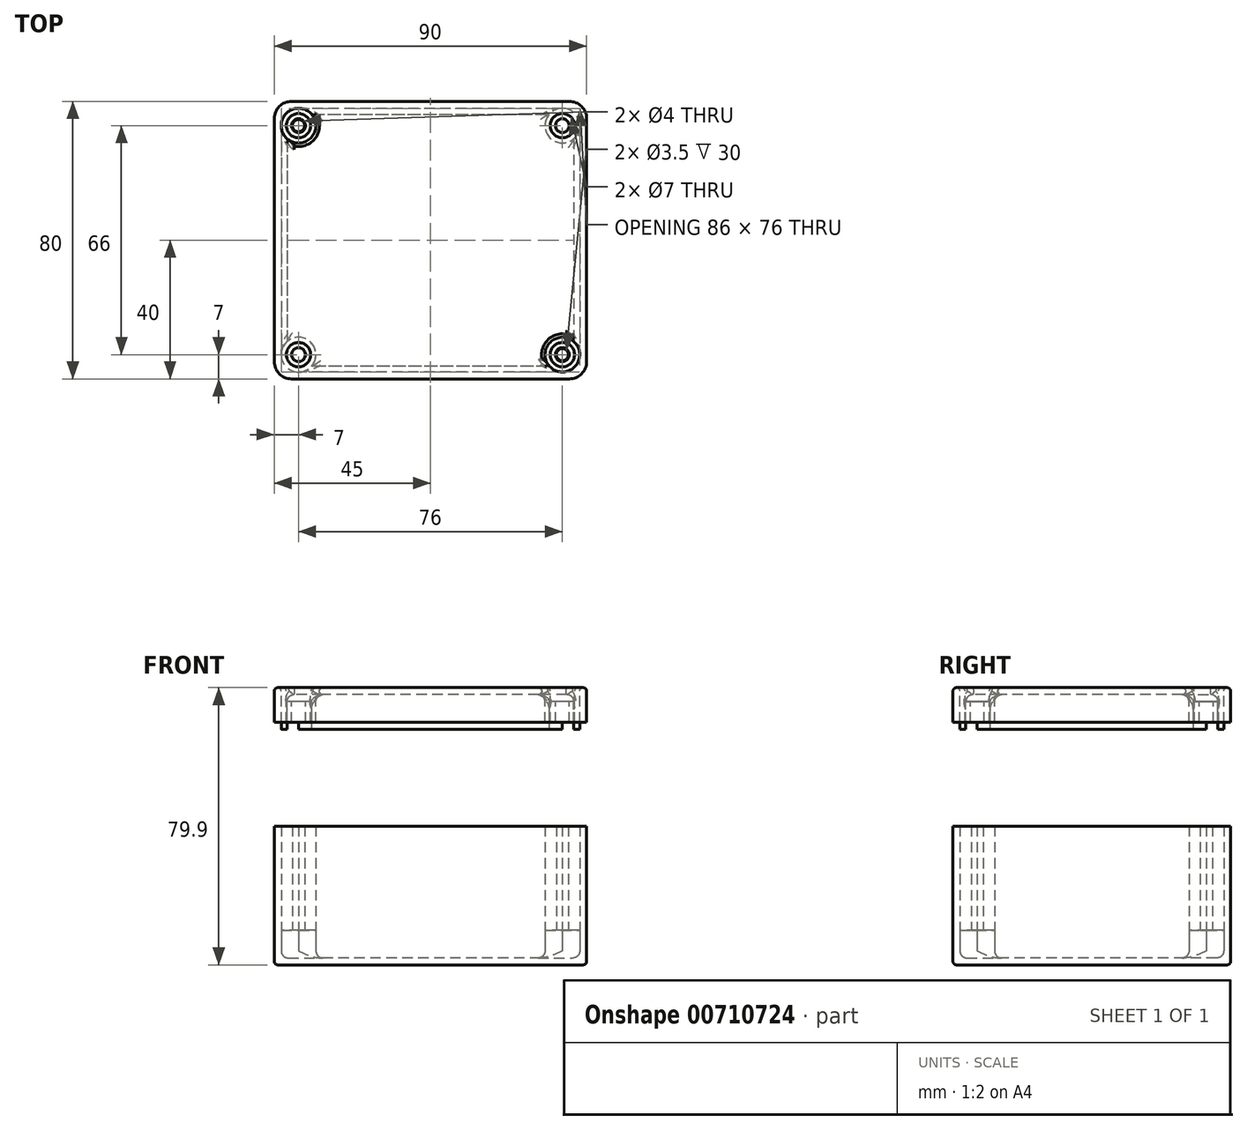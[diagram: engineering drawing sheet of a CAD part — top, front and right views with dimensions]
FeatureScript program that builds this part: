
annotation { "Feature Type Name" : "Feature", "Feature Type Description" : "" }
export const myFeature = defineFeature(function(context is Context, id is Id, definition is map)
    precondition{}
    {
        {
            var Q0;
            Q0=qCreatedBy(makeId("Top.planeOp"),FACE);
            var sketch = newSketch(context, id + "F0", { "sketchPlane" : qUnion([Q0])});
            skLineSegment(sketch, "E0.bottom", {"start": v(40, 40) * mm, "end": v(-40, 40) * mm});
            skLineSegment(sketch, "E0.top", {"start": v(40, -40) * mm, "end": v(-40, -40) * mm});
            skLineSegment(sketch, "E0.left", {"start": v(45, 35) * mm, "end": v(45, -35) * mm});
            skLineSegment(sketch, "E0.right", {"start": v(-45, 35) * mm, "end": v(-45, -35) * mm});
            skPoint(sketch, "E0.middle", {"position": v(0, 0) * mm});
            skPoint(sketch, "E1.visualSharp", {"position": v(-45, 40) * mm});
            skArc(sketch, "E1.filletArc", {"start": v(-40, 40) * mm, "mid": v(-43.54, 38.54) * mm, "end": v(-45, 35) * mm});
            skPoint(sketch, "E2.visualSharp", {"position": v(45, 40) * mm});
            skArc(sketch, "E2.filletArc", {"start": v(45, 35) * mm, "mid": v(43.54, 38.54) * mm, "end": v(40, 40) * mm});
            skPoint(sketch, "E3.visualSharp", {"position": v(-45, -40) * mm});
            skArc(sketch, "E3.filletArc", {"start": v(-45, -35) * mm, "mid": v(-43.54, -38.54) * mm, "end": v(-40, -40) * mm});
            skPoint(sketch, "E4.visualSharp", {"position": v(45, -40) * mm});
            skArc(sketch, "E4.filletArc", {"start": v(40, -40) * mm, "mid": v(43.54, -38.54) * mm, "end": v(45, -35) * mm});
            skLineSegment(sketch, "E5.0", {"start": v(38, -38) * mm, "end": v(-38, -38) * mm});
            skLineSegment(sketch, "E5.1", {"start": v(43, 33) * mm, "end": v(43, -33) * mm});
            skLineSegment(sketch, "E5.2", {"start": v(38, 38) * mm, "end": v(-38, 38) * mm});
            skLineSegment(sketch, "E5.3", {"start": v(-43, 33) * mm, "end": v(-43, -33) * mm});
            skPoint(sketch, "E6.visualSharp", {"position": v(43, 38) * mm});
            skArc(sketch, "E6.filletArc", {"start": v(43, 33) * mm, "mid": v(41.54, 36.54) * mm, "end": v(38, 38) * mm});
            skPoint(sketch, "E7.visualSharp", {"position": v(43, -38) * mm});
            skArc(sketch, "E7.filletArc", {"start": v(38, -38) * mm, "mid": v(41.54, -36.54) * mm, "end": v(43, -33) * mm});
            skPoint(sketch, "E8.visualSharp", {"position": v(-43, -38) * mm});
            skArc(sketch, "E8.filletArc", {"start": v(-43, -33) * mm, "mid": v(-41.54, -36.54) * mm, "end": v(-38, -38) * mm});
            skPoint(sketch, "E9.visualSharp", {"position": v(-43, 38) * mm});
            skArc(sketch, "E9.filletArc", {"start": v(-38, 38) * mm, "mid": v(-41.54, 36.54) * mm, "end": v(-43, 33) * mm});
            skLineSegment(sketch, "E10", {"start": v(0, 38) * mm, "end": v(0, -38) * mm, "construction": true});
            skCircle(sketch, "E11", {"center": v(-38, 33) * mm, "radius": 5 * mm});
            skCircle(sketch, "E12", {"center": v(-38, 33) * mm, "radius": 1.75 * mm});
            skLineSegment(sketch, "E13", {"start": v(-43, 0) * mm, "end": v(43, 0) * mm, "construction": true});
            skCircle(sketch, "E14.MirrorC", {"center": v(-38, -33) * mm, "radius": 5 * mm});
            skCircle(sketch, "E15.MirrorC", {"center": v(-38, -33) * mm, "radius": 1.75 * mm});
            skCircle(sketch, "E16.MirrorC", {"center": v(38, 33) * mm, "radius": 5 * mm});
            skCircle(sketch, "E17.MirrorC", {"center": v(38, 33) * mm, "radius": 1.75 * mm});
            skCircle(sketch, "E18.MirrorC", {"center": v(38, -33) * mm, "radius": 5 * mm});
            skCircle(sketch, "E19.MirrorC", {"center": v(38, -33) * mm, "radius": 1.75 * mm});
            skSolve(sketch);
        }
        {
            var Q0;
            {var subQ2=sQuery(id+"F0.wireOp",EDGE,"E5.0");Q0=makeQuery(id+"F0.imprint","IMPRINT",FACE,{"disambiguationData":[TD([[makeQuery(id+"F0.imprint","IMPRINT",EDGE,{"derivedFrom":subQ2}),-1.0]])]});}
            extrude(context, id + "F1", {"entities" : qUnion([Q0]), "depth" : 2 * mm, "offsetDistance" : 25 * mm});
        }
        {
            var Q0;
            Q0=makeQuery(id+"F0.imprint","IMPRINT",FACE,{"disambiguationData":[TD([[makeQuery(id+"F0.imprint","IMPRINT",EDGE,{"derivedFrom":sQuery(id+"F0.wireOp",EDGE,"E12")}),-1.0]])]});
            var Q1;
            Q1=makeQuery(id+"F0.imprint","IMPRINT",FACE,{"disambiguationData":[TD([[makeQuery(id+"F0.imprint","IMPRINT",EDGE,{"derivedFrom":sQuery(id+"F0.wireOp",EDGE,"E15.MirrorC")}),1.0]])]});
            var Q2;
            Q2=makeQuery(id+"F0.imprint","IMPRINT",FACE,{"disambiguationData":[TD([[makeQuery(id+"F0.imprint","IMPRINT",EDGE,{"derivedFrom":sQuery(id+"F0.wireOp",EDGE,"E0.bottom")}),1.0]])]});
            var Q3;
            Q3=makeQuery(id+"F0.imprint","IMPRINT",FACE,{"disambiguationData":[TD([[makeQuery(id+"F0.imprint","IMPRINT",EDGE,{"derivedFrom":sQuery(id+"F0.wireOp",EDGE,"E19.MirrorC")}),-1.0]])]});
            var Q4;
            Q4=makeQuery(id+"F0.imprint","IMPRINT",FACE,{"disambiguationData":[TD([[makeQuery(id+"F0.imprint","IMPRINT",EDGE,{"derivedFrom":sQuery(id+"F0.wireOp",EDGE,"E17.MirrorC")}),1.0]])]});
            extrude(context, id + "F2", {"entities" : qUnion([Q0, Q1, Q2, Q3, Q4]), "operationType" : NewBodyOperationType.ADD, "depth" : 40 * mm, "offsetDistance" : 25 * mm});
        }
        {
            var Q0;
            Q0=makeQuery(id+"F0.imprint","IMPRINT",FACE,{"disambiguationData":[TD([[makeQuery(id+"F0.imprint","IMPRINT",EDGE,{"derivedFrom":sQuery(id+"F0.wireOp",EDGE,"E17.MirrorC")}),-1.0]])]});
            var Q1;
            Q1=makeQuery(id+"F0.imprint","IMPRINT",FACE,{"disambiguationData":[TD([[makeQuery(id+"F0.imprint","IMPRINT",EDGE,{"derivedFrom":sQuery(id+"F0.wireOp",EDGE,"E19.MirrorC")}),1.0]])]});
            var Q2;
            Q2=makeQuery(id+"F0.imprint","IMPRINT",FACE,{"disambiguationData":[TD([[makeQuery(id+"F0.imprint","IMPRINT",EDGE,{"derivedFrom":sQuery(id+"F0.wireOp",EDGE,"E15.MirrorC")}),-1.0]])]});
            var Q3;
            Q3=makeQuery(id+"F0.imprint","IMPRINT",FACE,{"disambiguationData":[TD([[makeQuery(id+"F0.imprint","IMPRINT",EDGE,{"derivedFrom":sQuery(id+"F0.wireOp",EDGE,"E12")}),1.0]])]});
            extrude(context, id + "F3", {"entities" : qUnion([Q0, Q1, Q2, Q3]), "operationType" : NewBodyOperationType.ADD, "depth" : 10 * mm, "offsetDistance" : 25 * mm});
        }
        {
            var Q0;
            Q0=qCreatedBy(makeId("Top.planeOp"),FACE);
            cPlane(context, id + "F4", {"entities" : qUnion([Q0]), "cplaneType" : CPlaneType.OFFSET, "offset" : 79.9 * mm, "width" : 150 * mm, "height" : 150 * mm});
        }
        {
            var Q0;
            Q0=qCreatedBy(id+"F4.planeOp",FACE);
            var sketch = newSketch(context, id + "F5", { "sketchPlane" : qUnion([Q0])});
            skLineSegment(sketch, "E20.bottom", {"start": v(-40, 40) * mm, "end": v(40, 40) * mm});
            skLineSegment(sketch, "E20.top", {"start": v(-40, -40) * mm, "end": v(40, -40) * mm});
            skLineSegment(sketch, "E20.left", {"start": v(-45, 35) * mm, "end": v(-45, -35) * mm});
            skLineSegment(sketch, "E20.right", {"start": v(45, 35) * mm, "end": v(45, -35) * mm});
            skPoint(sketch, "E20.middle", {"position": v(0, 0) * mm});
            skPoint(sketch, "E21.visualSharp", {"position": v(-45, 40) * mm});
            skArc(sketch, "E21.filletArc", {"start": v(-40, 40) * mm, "mid": v(-43.54, 38.54) * mm, "end": v(-45, 35) * mm});
            skPoint(sketch, "E22.visualSharp", {"position": v(-45, -40) * mm});
            skArc(sketch, "E22.filletArc", {"start": v(-45, -35) * mm, "mid": v(-43.54, -38.54) * mm, "end": v(-40, -40) * mm});
            skPoint(sketch, "E23.visualSharp", {"position": v(45, -40) * mm});
            skArc(sketch, "E23.filletArc", {"start": v(40, -40) * mm, "mid": v(43.54, -38.54) * mm, "end": v(45, -35) * mm});
            skPoint(sketch, "E24.visualSharp", {"position": v(45, 40) * mm});
            skArc(sketch, "E24.filletArc", {"start": v(45, 35) * mm, "mid": v(43.54, 38.54) * mm, "end": v(40, 40) * mm});
            skLineSegment(sketch, "E25.0", {"start": v(-38, 38) * mm, "end": v(38, 38) * mm});
            skLineSegment(sketch, "E25.1", {"start": v(-43, 33) * mm, "end": v(-43, -33) * mm});
            skLineSegment(sketch, "E25.2", {"start": v(-38, -38) * mm, "end": v(38, -38) * mm});
            skLineSegment(sketch, "E25.3", {"start": v(43, 33) * mm, "end": v(43, -33) * mm});
            skPoint(sketch, "E26.visualSharp", {"position": v(-43, 38) * mm});
            skArc(sketch, "E26.filletArc", {"start": v(-38, 38) * mm, "mid": v(-41.54, 36.54) * mm, "end": v(-43, 33) * mm});
            skPoint(sketch, "E27.visualSharp", {"position": v(-43, -38) * mm});
            skArc(sketch, "E27.filletArc", {"start": v(-43, -33) * mm, "mid": v(-41.54, -36.54) * mm, "end": v(-38, -38) * mm});
            skPoint(sketch, "E28.visualSharp", {"position": v(43, -38) * mm});
            skArc(sketch, "E28.filletArc", {"start": v(38, -38) * mm, "mid": v(41.54, -36.54) * mm, "end": v(43, -33) * mm});
            skPoint(sketch, "E29.visualSharp", {"position": v(43, 38) * mm});
            skArc(sketch, "E29.filletArc", {"start": v(43, 33) * mm, "mid": v(41.54, 36.54) * mm, "end": v(38, 38) * mm});
            skCircle(sketch, "E30", {"center": v(-38, 33) * mm, "radius": 5 * mm});
            skCircle(sketch, "E31", {"center": v(-38, 33) * mm, "radius": 2 * mm});
            skLineSegment(sketch, "E32", {"start": v(0, 38) * mm, "end": v(0, -38) * mm, "construction": true});
            skLineSegment(sketch, "E33", {"start": v(-43, 0) * mm, "end": v(43, 0) * mm, "construction": true});
            skCircle(sketch, "E34.MirrorC", {"center": v(38, 33) * mm, "radius": 2 * mm});
            skCircle(sketch, "E35.MirrorC", {"center": v(38, 33) * mm, "radius": 5 * mm});
            skCircle(sketch, "E36.MirrorC", {"center": v(-38, -33) * mm, "radius": 5 * mm});
            skCircle(sketch, "E37.MirrorC", {"center": v(-38, -33) * mm, "radius": 2 * mm});
            skCircle(sketch, "E38.MirrorC", {"center": v(38, -33) * mm, "radius": 2 * mm});
            skCircle(sketch, "E39.MirrorC", {"center": v(38, -33) * mm, "radius": 5 * mm});
            skLineSegment(sketch, "E40", {"start": v(-41.3, 29.24) * mm, "end": v(-41.3, -29.24) * mm});
            skLineSegment(sketch, "E41", {"start": v(-34.24, 36.3) * mm, "end": v(34.24, 36.3) * mm});
            skLineSegment(sketch, "E42", {"start": v(41.3, 29.24) * mm, "end": v(41.3, -29.24) * mm});
            skLineSegment(sketch, "E43", {"start": v(34.24, -36.3) * mm, "end": v(-34.24, -36.3) * mm});
            skCircle(sketch, "E44", {"center": v(-38, -33) * mm, "radius": 3.5 * mm});
            skCircle(sketch, "E45.MirrorC", {"center": v(38, -33) * mm, "radius": 3.5 * mm});
            skCircle(sketch, "E46.MirrorC", {"center": v(-38, 33) * mm, "radius": 3.5 * mm});
            skCircle(sketch, "E47.MirrorC", {"center": v(38, 33) * mm, "radius": 3.5 * mm});
            skSolve(sketch);
        }
        {
            var Q0;
            Q0=makeQuery(id+"F5.imprint","IMPRINT",FACE,{"disambiguationData":[TD([[makeQuery(id+"F5.imprint","IMPRINT",EDGE,{"derivedFrom":sQuery(id+"F5.wireOp",EDGE,"E46.MirrorC")}),1.0]])]});
            var Q1;
            Q1=makeQuery(id+"F5.imprint","IMPRINT",FACE,{"disambiguationData":[TD([[makeQuery(id+"F5.imprint","IMPRINT",EDGE,{"derivedFrom":sQuery(id+"F5.wireOp",EDGE,"E20.bottom")}),-1.0]])]});
            var Q2;
            Q2=makeQuery(id+"F5.imprint","IMPRINT",FACE,{"disambiguationData":[TD([[makeQuery(id+"F5.imprint","IMPRINT",EDGE,{"derivedFrom":sQuery(id+"F5.wireOp",EDGE,"E44")}),-1.0]])]});
            var Q3;
            Q3=makeQuery(id+"F5.imprint","IMPRINT",FACE,{"disambiguationData":[TD([[makeQuery(id+"F5.imprint","IMPRINT",EDGE,{"derivedFrom":sQuery(id+"F5.wireOp",EDGE,"E45.MirrorC")}),1.0]])]});
            var Q4;
            Q4=makeQuery(id+"F5.imprint","IMPRINT",FACE,{"disambiguationData":[TD([[makeQuery(id+"F5.imprint","IMPRINT",EDGE,{"derivedFrom":sQuery(id+"F5.wireOp",EDGE,"E47.MirrorC")}),-1.0]])]});
            extrude(context, id + "F6", {"entities" : qUnion([Q0, Q1, Q2, Q3, Q4]), "depth" : -10 * mm, "offsetDistance" : 25 * mm});
        }
        {
            var Q0;
            Q0=makeQuery(id+"F5.imprint","IMPRINT",FACE,{"disambiguationData":[TD([[makeQuery(id+"F5.imprint","IMPRINT",EDGE,{"derivedFrom":sQuery(id+"F5.wireOp",EDGE,"E31")}),-1.0]])]});
            var Q1;
            Q1=makeQuery(id+"F5.imprint","IMPRINT",FACE,{"disambiguationData":[TD([[makeQuery(id+"F5.imprint","IMPRINT",EDGE,{"derivedFrom":sQuery(id+"F5.wireOp",EDGE,"E37.MirrorC")}),1.0]])]});
            var Q2;
            Q2=makeQuery(id+"F5.imprint","IMPRINT",FACE,{"disambiguationData":[TD([[makeQuery(id+"F5.imprint","IMPRINT",EDGE,{"derivedFrom":sQuery(id+"F5.wireOp",EDGE,"E38.MirrorC")}),-1.0]])]});
            var Q3;
            Q3=makeQuery(id+"F5.imprint","IMPRINT",FACE,{"disambiguationData":[TD([[makeQuery(id+"F5.imprint","IMPRINT",EDGE,{"derivedFrom":sQuery(id+"F5.wireOp",EDGE,"E34.MirrorC")}),1.0]])]});
            extrude(context, id + "F7", {"entities" : qUnion([Q0, Q1, Q2, Q3]), "operationType" : NewBodyOperationType.ADD, "depth" : -10 * mm, "offsetDistance" : 25 * mm});
        }
        {
            var Q0;
            Q0=makeQuery(id+"F5.imprint","IMPRINT",FACE,{"disambiguationData":[TD([[makeQuery(id+"F5.imprint","IMPRINT",EDGE,{"derivedFrom":sQuery(id+"F5.wireOp",EDGE,"E31")}),-1.0]])]});
            var Q1;
            Q1=makeQuery(id+"F5.imprint","IMPRINT",FACE,{"disambiguationData":[TD([[makeQuery(id+"F5.imprint","IMPRINT",EDGE,{"derivedFrom":sQuery(id+"F5.wireOp",EDGE,"E37.MirrorC")}),1.0]])]});
            var Q2;
            Q2=makeQuery(id+"F5.imprint","IMPRINT",FACE,{"disambiguationData":[TD([[makeQuery(id+"F5.imprint","IMPRINT",EDGE,{"derivedFrom":sQuery(id+"F5.wireOp",EDGE,"E38.MirrorC")}),-1.0]])]});
            var Q3;
            Q3=makeQuery(id+"F5.imprint","IMPRINT",FACE,{"disambiguationData":[TD([[makeQuery(id+"F5.imprint","IMPRINT",EDGE,{"derivedFrom":sQuery(id+"F5.wireOp",EDGE,"E34.MirrorC")}),1.0]])]});
            extrude(context, id + "F8", {"entities" : qUnion([Q0, Q1, Q2, Q3]), "operationType" : NewBodyOperationType.REMOVE, "oppositeDirection" : true, "depth" : 4 * mm, "offsetDistance" : 25 * mm});
        }
        {
            var Q0;
            {var subQ0=sQuery(id+"F5.wireOp",EDGE,"E25.0");Q0=makeQuery(id+"F5.imprint","IMPRINT",FACE,{"disambiguationData":[TD([[makeQuery(id+"F5.imprint","IMPRINT",EDGE,{"derivedFrom":subQ0}),-1.0]])]});}
            var Q1;
            {var subQ0=sQuery(id+"F5.wireOp",EDGE,"E25.1");Q1=makeQuery(id+"F5.imprint","IMPRINT",FACE,{"disambiguationData":[TD([[makeQuery(id+"F5.imprint","IMPRINT",EDGE,{"derivedFrom":subQ0}),1.0]])]});}
            var Q2;
            {var subQ0=sQuery(id+"F5.wireOp",EDGE,"E25.2");Q2=makeQuery(id+"F5.imprint","IMPRINT",FACE,{"disambiguationData":[TD([[makeQuery(id+"F5.imprint","IMPRINT",EDGE,{"derivedFrom":subQ0}),1.0]])]});}
            var Q3;
            {var subQ0=sQuery(id+"F5.wireOp",EDGE,"E25.3");Q3=makeQuery(id+"F5.imprint","IMPRINT",FACE,{"disambiguationData":[TD([[makeQuery(id+"F5.imprint","IMPRINT",EDGE,{"derivedFrom":subQ0}),-1.0]])]});}
            extrude(context, id + "F9", {"entities" : qUnion([Q0, Q1, Q2, Q3]), "operationType" : NewBodyOperationType.ADD, "depth" : -12 * mm, "offsetDistance" : 25 * mm});
        }
        {
            var Q0;
            {var subQ5=sQuery(id+"F5.wireOp",EDGE,"E40");Q0=makeQuery(id+"F5.imprint","IMPRINT",FACE,{"disambiguationData":[TD([[makeQuery(id+"F5.imprint","IMPRINT",EDGE,{"derivedFrom":subQ5}),1.0]])]});}
            extrude(context, id + "F10", {"entities" : qUnion([Q0]), "operationType" : NewBodyOperationType.ADD, "depth" : -2 * mm, "offsetDistance" : 25 * mm});
        }
        {
            var Q0;
            Q0=makeQuery(id+"F1.opExtrude","CAP_FACE",FACE,{"disambiguationData":[OSD([sQuery(id+"F0.wireOp",EDGE,"E5.0"),sQuery(id+"F0.wireOp",EDGE,"E5.1"),sQuery(id+"F0.wireOp",EDGE,"E5.2"),sQuery(id+"F0.wireOp",EDGE,"E5.3"),sQuery(id+"F0.wireOp",EDGE,"E11"),sQuery(id+"F0.wireOp",EDGE,"E14.MirrorC"),sQuery(id+"F0.wireOp",EDGE,"E16.MirrorC"),sQuery(id+"F0.wireOp",EDGE,"E18.MirrorC")])],"isStart":false});
            fillet(context, id + "F11", {"entities" : qUnion([Q0]), "radius" : 2 * mm, "tangentPropagation" : true, "allowEdgeOverflow" : false});
        }
        {
            var Q0;
            {var subQ0=sQuery(id+"F0.wireOp",EDGE,"E19.MirrorC");var subQ1=sQuery(id+"F0.wireOp",EDGE,"E17.MirrorC");var subQ2=sQuery(id+"F0.wireOp",EDGE,"E15.MirrorC");var subQ3=sQuery(id+"F0.wireOp",EDGE,"E12");var subQ4=sQuery(id+"F0.wireOp",EDGE,"E18.MirrorC");var subQ5=sQuery(id+"F0.wireOp",EDGE,"E16.MirrorC");var subQ6=sQuery(id+"F0.wireOp",EDGE,"E14.MirrorC");var subQ7=sQuery(id+"F0.wireOp",EDGE,"E11");var subQ8=sQuery(id+"F0.wireOp",EDGE,"E5.3");var subQ9=sQuery(id+"F0.wireOp",EDGE,"E5.2");var subQ10=sQuery(id+"F0.wireOp",EDGE,"E5.1");var subQ11=sQuery(id+"F0.wireOp",EDGE,"E5.0");Q0=makeQuery(id+"F3.boolean.opBoolean","MERGE",FACE,{"derivedFrom":[makeQuery(id+"F2.boolean.opBoolean","MERGE",FACE,{"derivedFrom":[makeQuery(id+"F1.opExtrude","CAP_FACE",FACE,{"disambiguationData":[OSD([subQ11,subQ10,subQ9,subQ8,subQ7,subQ6,subQ5,subQ4])],"isStart":true}),makeQuery(id+"F2.opExtrude","CAP_FACE",FACE,{"disambiguationData":[OSD([sQuery(id+"F0.wireOp",EDGE,"E0.bottom"),sQuery(id+"F0.wireOp",EDGE,"E0.top"),sQuery(id+"F0.wireOp",EDGE,"E0.left"),sQuery(id+"F0.wireOp",EDGE,"E0.right"),sQuery(id+"F0.wireOp",EDGE,"E1.filletArc"),sQuery(id+"F0.wireOp",EDGE,"E2.filletArc"),sQuery(id+"F0.wireOp",EDGE,"E3.filletArc"),sQuery(id+"F0.wireOp",EDGE,"E4.filletArc"),subQ11,subQ10,subQ9,subQ8,subQ7,subQ3,subQ6,subQ2,subQ5,subQ1,subQ4,subQ0])],"isStart":true})]}),makeQuery(id+"F3.opExtrude","CAP_FACE",FACE,{"disambiguationData":[OSD([subQ3])],"isStart":true}),makeQuery(id+"F3.opExtrude","CAP_FACE",FACE,{"disambiguationData":[OSD([subQ2])],"isStart":true}),makeQuery(id+"F3.opExtrude","CAP_FACE",FACE,{"disambiguationData":[OSD([subQ1])],"isStart":true}),makeQuery(id+"F3.opExtrude","CAP_FACE",FACE,{"disambiguationData":[OSD([subQ0])],"isStart":true})]});}
            fillet(context, id + "F12", {"entities" : qUnion([Q0]), "radius" : 1 * mm, "tangentPropagation" : true, "allowEdgeOverflow" : false});
        }
        {
            var Q0;
            Q0=makeQuery(id+"F10.opExtrude","CAP_FACE",FACE,{"disambiguationData":[OSD([sQuery(id+"F5.wireOp",EDGE,"E30"),sQuery(id+"F5.wireOp",EDGE,"E35.MirrorC"),sQuery(id+"F5.wireOp",EDGE,"E36.MirrorC"),sQuery(id+"F5.wireOp",EDGE,"E39.MirrorC"),sQuery(id+"F5.wireOp",EDGE,"E40"),sQuery(id+"F5.wireOp",EDGE,"E41"),sQuery(id+"F5.wireOp",EDGE,"E42"),sQuery(id+"F5.wireOp",EDGE,"E43")])],"isStart":false});
            fillet(context, id + "F13", {"entities" : qUnion([Q0]), "radius" : 2 * mm, "tangentPropagation" : true, "allowEdgeOverflow" : false});
        }
        {
            var Q0;
            {var subQ0=sQuery(id+"F5.wireOp",EDGE,"E43");var subQ1=sQuery(id+"F5.wireOp",EDGE,"E42");var subQ2=sQuery(id+"F5.wireOp",EDGE,"E41");var subQ3=sQuery(id+"F5.wireOp",EDGE,"E40");var subQ4=sQuery(id+"F5.wireOp",EDGE,"E39.MirrorC");var subQ5=sQuery(id+"F5.wireOp",EDGE,"E36.MirrorC");var subQ6=sQuery(id+"F5.wireOp",EDGE,"E35.MirrorC");var subQ7=sQuery(id+"F5.wireOp",EDGE,"E30");var subQ8=sQuery(id+"F5.wireOp",EDGE,"E25.3");var subQ9=sQuery(id+"F5.wireOp",EDGE,"E25.2");var subQ10=sQuery(id+"F5.wireOp",EDGE,"E25.1");var subQ11=sQuery(id+"F5.wireOp",EDGE,"E25.0");var subQ12=sQuery(id+"F5.wireOp",EDGE,"E45.MirrorC");var subQ13=sQuery(id+"F5.wireOp",EDGE,"E44");var subQ14=sQuery(id+"F5.wireOp",EDGE,"E47.MirrorC");var subQ15=sQuery(id+"F5.wireOp",EDGE,"E46.MirrorC");Q0=makeQuery(id+"F10.boolean.opBoolean","MERGE",FACE,{"derivedFrom":[makeQuery(id+"F9.boolean.opBoolean","MERGE",FACE,{"derivedFrom":[makeQuery(id+"F7.boolean.opBoolean","MERGE",FACE,{"derivedFrom":[makeQuery(id+"F6.opExtrude","CAP_FACE",FACE,{"disambiguationData":[OSD([sQuery(id+"F5.wireOp",EDGE,"E20.bottom"),sQuery(id+"F5.wireOp",EDGE,"E20.top"),sQuery(id+"F5.wireOp",EDGE,"E20.left"),sQuery(id+"F5.wireOp",EDGE,"E20.right"),sQuery(id+"F5.wireOp",EDGE,"E21.filletArc"),sQuery(id+"F5.wireOp",EDGE,"E22.filletArc"),sQuery(id+"F5.wireOp",EDGE,"E23.filletArc"),sQuery(id+"F5.wireOp",EDGE,"E24.filletArc"),subQ11,subQ10,subQ9,subQ8,subQ7,subQ6,subQ5,subQ4,subQ13,subQ12,subQ15,subQ14])],"isStart":true}),makeQuery(id+"F7.opExtrude","CAP_FACE",FACE,{"disambiguationData":[OSD([sQuery(id+"F5.wireOp",EDGE,"E31"),subQ15])],"isStart":true}),makeQuery(id+"F7.opExtrude","CAP_FACE",FACE,{"disambiguationData":[OSD([sQuery(id+"F5.wireOp",EDGE,"E34.MirrorC"),subQ14])],"isStart":true}),makeQuery(id+"F7.opExtrude","CAP_FACE",FACE,{"disambiguationData":[OSD([sQuery(id+"F5.wireOp",EDGE,"E37.MirrorC"),subQ13])],"isStart":true}),makeQuery(id+"F7.opExtrude","CAP_FACE",FACE,{"disambiguationData":[OSD([sQuery(id+"F5.wireOp",EDGE,"E38.MirrorC"),subQ12])],"isStart":true})]}),makeQuery(id+"F9.opExtrude","CAP_FACE",FACE,{"disambiguationData":[OSD([subQ11,subQ7,subQ6,subQ2])],"isStart":true}),makeQuery(id+"F9.opExtrude","CAP_FACE",FACE,{"disambiguationData":[OSD([subQ10,subQ7,subQ5,subQ3])],"isStart":true}),makeQuery(id+"F9.opExtrude","CAP_FACE",FACE,{"disambiguationData":[OSD([subQ9,subQ5,subQ4,subQ0])],"isStart":true}),makeQuery(id+"F9.opExtrude","CAP_FACE",FACE,{"disambiguationData":[OSD([subQ8,subQ6,subQ4,subQ1])],"isStart":true})]}),makeQuery(id+"F10.opExtrude","CAP_FACE",FACE,{"disambiguationData":[OSD([subQ7,subQ6,subQ5,subQ4,subQ3,subQ2,subQ1,subQ0])],"isStart":true})]});}
            var Q1;
            Q1=makeQuery(id+"F8.boolean.opBoolean","COPY",EDGE,{"derivedFrom":makeQuery(id+"F8.opExtrude","CAP_EDGE",EDGE,{"disambiguationData":[OSD([sQuery(id+"F5.wireOp",EDGE,"E45.MirrorC")])],"isStart":true})});
            fillet(context, id + "F14", {"entities" : qUnion([Q0, Q1]), "radius" : 1 * mm, "tangentPropagation" : true, "allowEdgeOverflow" : false});
        }
    });
